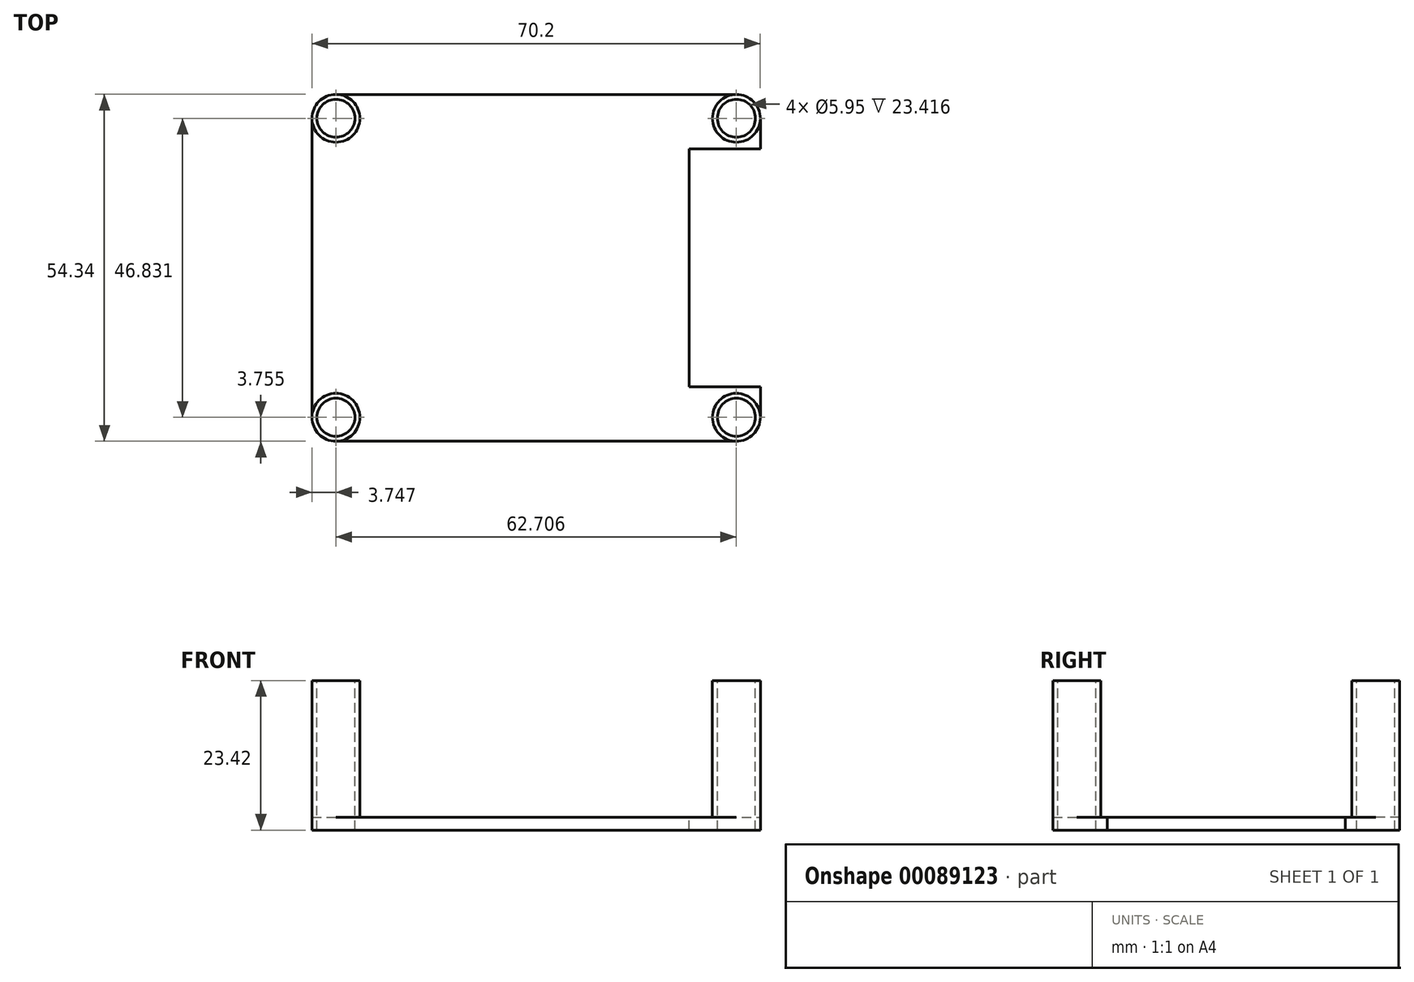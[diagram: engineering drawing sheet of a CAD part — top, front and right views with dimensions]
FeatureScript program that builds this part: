
annotation { "Feature Type Name" : "Feature", "Feature Type Description" : "" }
export const myFeature = defineFeature(function(context is Context, id is Id, definition is map)
    precondition{}
    {
        {
            var Q0;
            Q0=qCreatedBy(makeId("Top.planeOp"),FACE);
            var sketch = newSketch(context, id + "F0", { "sketchPlane" : qUnion([Q0])});
            skLineSegment(sketch, "E0.bottom", {"start": v(31.35, -27.17) * mm, "end": v(-31.35, -27.17) * mm});
            skLineSegment(sketch, "E0.top", {"start": v(31.35, 27.17) * mm, "end": v(-31.35, 27.17) * mm});
            skLineSegment(sketch, "E0.left", {"start": v(35.1, -23.42) * mm, "end": v(35.1, 23.42) * mm});
            skLineSegment(sketch, "E0.right", {"start": v(-35.1, -23.42) * mm, "end": v(-35.1, 23.42) * mm});
            skPoint(sketch, "E0.middle", {"position": v(0, 0) * mm});
            skPoint(sketch, "E1.visualSharp", {"position": v(35.1, 27.17) * mm});
            skArc(sketch, "E1.filletArc", {"start": v(35.1, 23.42) * mm, "mid": v(34, 26.07) * mm, "end": v(31.35, 27.17) * mm});
            skPoint(sketch, "E2.visualSharp", {"position": v(35.1, -27.17) * mm});
            skArc(sketch, "E2.filletArc", {"start": v(31.35, -27.17) * mm, "mid": v(34, -26.07) * mm, "end": v(35.1, -23.42) * mm});
            skPoint(sketch, "E3.visualSharp", {"position": v(-35.1, -27.17) * mm});
            skArc(sketch, "E3.filletArc", {"start": v(-35.1, -23.42) * mm, "mid": v(-34, -26.07) * mm, "end": v(-31.35, -27.17) * mm});
            skPoint(sketch, "E4.visualSharp", {"position": v(-35.1, 27.17) * mm});
            skArc(sketch, "E4.filletArc", {"start": v(-31.35, 27.17) * mm, "mid": v(-34, 26.07) * mm, "end": v(-35.1, 23.42) * mm});
            skSolve(sketch);
        }
        {
            var Q0;
            Q0 = qSketchRegion(id + "F0", true);
            extrude(context, id + "F1", {"entities" : qUnion([Q0]), "depth" : 2 * mm});
        }
        {
            var Q0;
            Q0=makeQuery(id+"F1.opExtrude","CAP_FACE",FACE,{"disambiguationData":[OSD([sQuery(id+"F0.wireOp",EDGE,"E0.bottom"),sQuery(id+"F0.wireOp",EDGE,"E0.top"),sQuery(id+"F0.wireOp",EDGE,"E0.left"),sQuery(id+"F0.wireOp",EDGE,"E0.right"),sQuery(id+"F0.wireOp",EDGE,"E1.filletArc"),sQuery(id+"F0.wireOp",EDGE,"E2.filletArc"),sQuery(id+"F0.wireOp",EDGE,"E3.filletArc"),sQuery(id+"F0.wireOp",EDGE,"E4.filletArc")])],"isStart":false});
            var sketch = newSketch(context, id + "F2", { "sketchPlane" : qUnion([Q0])});
            skCircle(sketch, "E5", {"center": v(-31.35, 23.42) * mm, "radius": 3.75 * mm});
            skCircle(sketch, "E6.MirrorC", {"center": v(31.35, 23.42) * mm, "radius": 3.75 * mm});
            skCircle(sketch, "E7.MirrorC", {"center": v(-31.35, -23.42) * mm, "radius": 3.75 * mm});
            skCircle(sketch, "E8.MirrorC", {"center": v(31.35, -23.42) * mm, "radius": 3.75 * mm});
            skSolve(sketch);
        }
        {
            var Q0;
            Q0 = qSketchRegion(id + "F2", true);
            extrude(context, id + "F3", {"entities" : qUnion([Q0]), "operationType" : NewBodyOperationType.ADD, "depth" : 21.42 * mm});
        }
        {
            var Q0;
            Q0=makeQuery(id+"F3.opExtrude","CAP_FACE",FACE,{"disambiguationData":[OSD([sQuery(id+"F2.wireOp",EDGE,"E5")])],"isStart":false});
            var sketch = newSketch(context, id + "F4", { "sketchPlane" : qUnion([Q0])});
            skCircle(sketch, "E9", {"center": v(-31.35, 23.42) * mm, "radius": 2.97 * mm});
            skCircle(sketch, "E10.MirrorC", {"center": v(31.35, 23.42) * mm, "radius": 2.97 * mm});
            skCircle(sketch, "E11.MirrorC", {"center": v(31.35, -23.42) * mm, "radius": 2.97 * mm});
            skCircle(sketch, "E12.MirrorC", {"center": v(-31.35, -23.42) * mm, "radius": 2.97 * mm});
            skSolve(sketch);
        }
        {
            var Q0;
            Q0 = qSketchRegion(id + "F4", true);
            extrude(context, id + "F5", {"entities" : qUnion([Q0]), "operationType" : NewBodyOperationType.REMOVE, "endBound" : BoundingType.THROUGH_ALL, "oppositeDirection" : true, "depth" : 25 * mm});
        }
        {
            var Q0;
            Q0=makeQuery(id+"F1.opExtrude","CAP_FACE",FACE,{"disambiguationData":[OSD([sQuery(id+"F0.wireOp",EDGE,"E0.bottom"),sQuery(id+"F0.wireOp",EDGE,"E0.top"),sQuery(id+"F0.wireOp",EDGE,"E0.left"),sQuery(id+"F0.wireOp",EDGE,"E0.right"),sQuery(id+"F0.wireOp",EDGE,"E1.filletArc"),sQuery(id+"F0.wireOp",EDGE,"E2.filletArc"),sQuery(id+"F0.wireOp",EDGE,"E3.filletArc"),sQuery(id+"F0.wireOp",EDGE,"E4.filletArc")])],"isStart":false});
            var sketch = newSketch(context, id + "F6", { "sketchPlane" : qUnion([Q0])});
            skLineSegment(sketch, "E13", {"start": v(23.95, 0) * mm, "end": v(23.95, 18.65) * mm});
            skLineSegment(sketch, "E14.MirrorCS", {"start": v(23.95, 0) * mm, "end": v(23.95, -18.65) * mm});
            skLineSegment(sketch, "E15", {"start": v(23.95, 18.65) * mm, "end": v(35.1, 18.65) * mm});
            skLineSegment(sketch, "E16", {"start": v(23.95, -18.65) * mm, "end": v(35.1, -18.65) * mm});
            skLineSegment(sketch, "E17", {"start": v(35.1, 18.65) * mm, "end": v(35.1, -18.65) * mm});
            skSolve(sketch);
        }
        {
            var Q0;
            Q0 = qSketchRegion(id + "F6", true);
            extrude(context, id + "F7", {"entities" : qUnion([Q0]), "operationType" : NewBodyOperationType.REMOVE, "endBound" : BoundingType.THROUGH_ALL, "oppositeDirection" : true, "depth" : 25 * mm});
        }
    });
